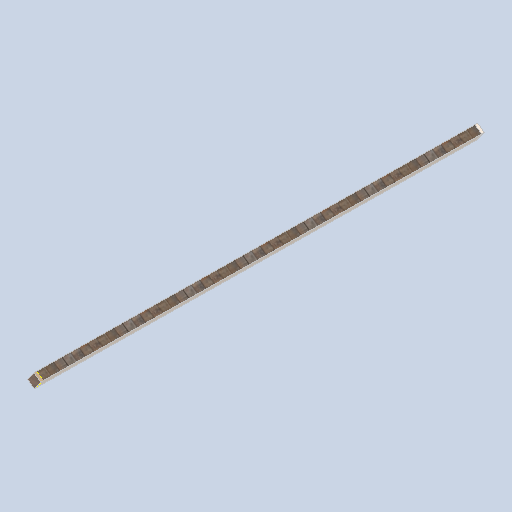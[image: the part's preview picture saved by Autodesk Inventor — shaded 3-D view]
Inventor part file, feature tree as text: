
AUTODESK INVENTOR PART (.ipt)
format: ipt  version: 2024.2 (Build 282272000, 272)  size: 135,168 bytes
history: native  units: in
note: dims shown in document units (in); Inventor stores cm internally (conversion verified against a paired STEP export)
features: sketch x5, other x3, plane x2
ambient origin geometry x8: Origin, YZ Plane, XZ Plane, XY Plane, X Axis, Y Axis, Z Axis, Center Point
bodies: Solid1 (feature_tree)
feature tree (10):
  other  "support_beam_segment_0106_MIR.ipt"
  other  "Solid1::support_beam_segment_0106_MIR.ipt"
  other  "TaggingFeature1"
  sketch  "Sketch1"  dims[d0=0.3937in]
  sketch  "Sketch2"
  sketch  "Sketch3"
  sketch  "Sketch4"
  sketch  "Sketch5"
  plane  "Work Plane1"
  plane  "Work Plane2"
